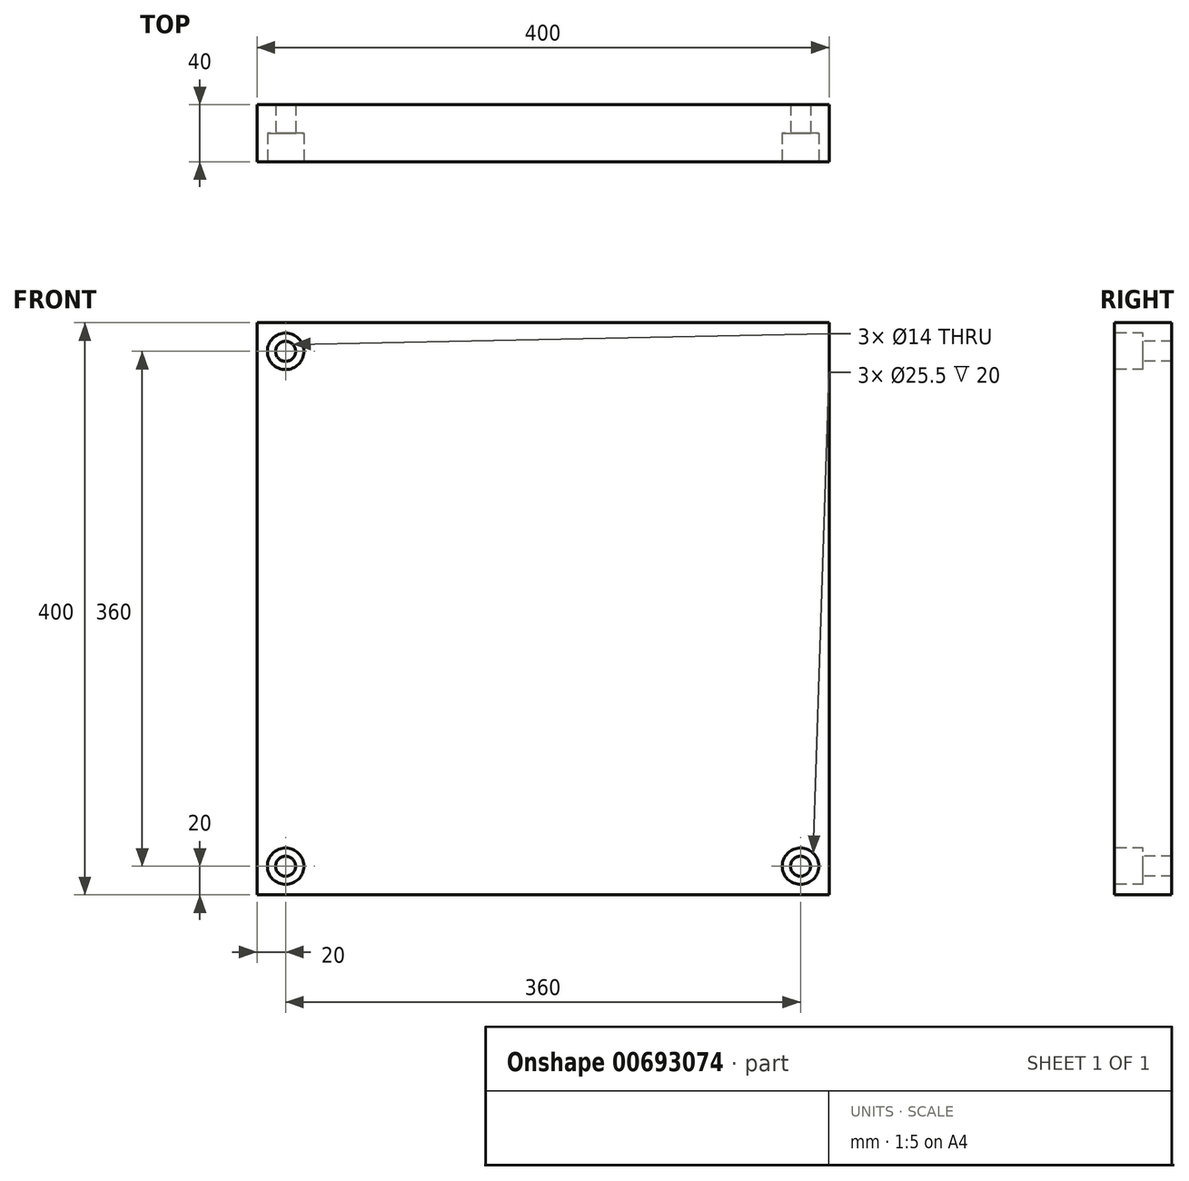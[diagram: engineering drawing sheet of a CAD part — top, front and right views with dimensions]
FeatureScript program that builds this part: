
annotation { "Feature Type Name" : "Feature", "Feature Type Description" : "" }
export const myFeature = defineFeature(function(context is Context, id is Id, definition is map)
    precondition{}
    {
        {
            var Q0;
            Q0=qCreatedBy(makeId("Front.planeOp"),FACE);
            var sketch = newSketch(context, id + "F0", { "sketchPlane" : qUnion([Q0])});
            skLineSegment(sketch, "E0.bottom", {"start": v(0, 0) * mm, "end": v(400, 0) * mm});
            skLineSegment(sketch, "E0.top", {"start": v(0, 400) * mm, "end": v(400, 400) * mm});
            skLineSegment(sketch, "E0.left", {"start": v(0, 0) * mm, "end": v(0, 400) * mm});
            skLineSegment(sketch, "E0.right", {"start": v(400, 0) * mm, "end": v(400, 400) * mm});
            skSolve(sketch);
        }
        {
            var Q0;
            Q0=makeQuery(id+"F0.imprint","IMPRINT",FACE,{"disambiguationData":[TD([[makeQuery(id+"F0.imprint","IMPRINT",EDGE,{"derivedFrom":sQuery(id+"F0.wireOp",EDGE,"E0.bottom")}),1.0]])]});
            extrude(context, id + "F1", {"entities" : qUnion([Q0]), "depth" : 40 * mm, "offsetDistance" : 25.4 * mm});
        }
        {
            var Q0;
            Q0=makeQuery(id+"F1.opExtrude","CAP_FACE",FACE,{"disambiguationData":[OSD([sQuery(id+"F0.wireOp",EDGE,"E0.bottom"),sQuery(id+"F0.wireOp",EDGE,"E0.top"),sQuery(id+"F0.wireOp",EDGE,"E0.left"),sQuery(id+"F0.wireOp",EDGE,"E0.right")])],"isStart":false});
            var sketch = newSketch(context, id + "F2", { "sketchPlane" : qUnion([Q0])});
            skLineSegment(sketch, "E1", {"start": v(0, 400) * mm, "end": v(20, 400) * mm});
            skLineSegment(sketch, "E2", {"start": v(20, 400) * mm, "end": v(20, 380) * mm});
            skLineSegment(sketch, "E3", {"start": v(0, 200) * mm, "end": v(66.66, 200) * mm});
            skLineSegment(sketch, "E4", {"start": v(200, 400) * mm, "end": v(200, 325.4) * mm});
            skLineSegment(sketch, "E5.MirrorCS", {"start": v(380, 400) * mm, "end": v(380, 380) * mm});
            skLineSegment(sketch, "E6.MirrorCS", {"start": v(20, 0) * mm, "end": v(20, 20) * mm});
            skLineSegment(sketch, "E7.MirrorCS", {"start": v(380, 0) * mm, "end": v(380, 20) * mm});
            skSolve(sketch);
        }
        {
            var Q0;
            Q0=sQuery(id+"F2.wireOp",VERTEX,"E2.end");
            var Q1;
            Q1=sQuery(id+"F2.wireOp",VERTEX,"E5.MirrorCS.end");
            var Q2;
            Q2=sQuery(id+"F2.wireOp",VERTEX,"E7.MirrorCS.end");
            var Q3;
            Q3=sQuery(id+"F2.wireOp",VERTEX,"E6.MirrorCS.end");
            var Q4;
            Q4=makeQuery(id+"F1.opExtrude","SWEPT_BODY",BODY,{"disambiguationData":[OSD([sQuery(id+"F0.wireOp",EDGE,"E0.bottom"),sQuery(id+"F0.wireOp",EDGE,"E0.top"),sQuery(id+"F0.wireOp",EDGE,"E0.left"),sQuery(id+"F0.wireOp",EDGE,"E0.right")])]});
            hole(context, id + "F3", {"style" : HoleStyle.C_BORE, "endStyle" : HoleEndStyle.THROUGH, "holeDiameter" : 14 * mm, "cBoreDiameter" : 25.5 * mm, "cBoreDepth" : 20 * mm, "majorDiameter" : 16 * mm, "tappedDepth" : 19.38 * mm, "tapClearance" : 3, "locations" : qUnion([Q0, Q1, Q2, Q3]), "scope" : qUnion([Q4])});
        }
    });
